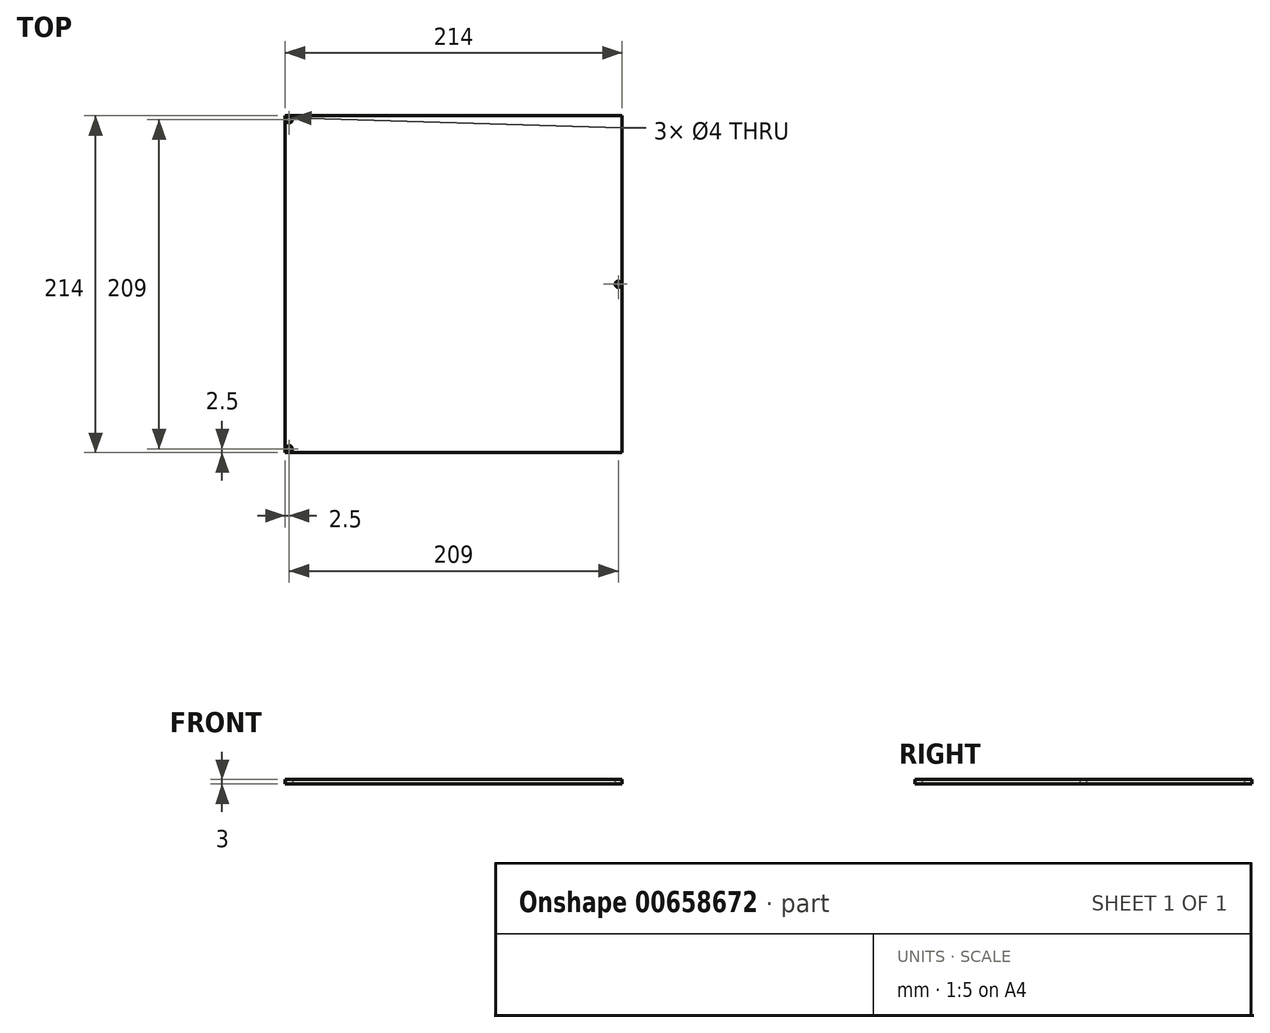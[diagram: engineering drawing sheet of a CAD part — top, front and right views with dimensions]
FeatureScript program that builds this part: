
annotation { "Feature Type Name" : "Feature", "Feature Type Description" : "" }
export const myFeature = defineFeature(function(context is Context, id is Id, definition is map)
    precondition{}
    {
        {
            var Q0;
            Q0=qCreatedBy(makeId("Top.planeOp"),FACE);
            var sketch = newSketch(context, id + "F0", { "sketchPlane" : qUnion([Q0])});
            skLineSegment(sketch, "E0.bottom", {"start": v(107, -107) * mm, "end": v(-107, -107) * mm});
            skLineSegment(sketch, "E0.top", {"start": v(107, 107) * mm, "end": v(-107, 107) * mm});
            skLineSegment(sketch, "E0.left", {"start": v(107, -107) * mm, "end": v(107, 107) * mm});
            skLineSegment(sketch, "E0.right", {"start": v(-107, -107) * mm, "end": v(-107, 107) * mm});
            skPoint(sketch, "E0.middle", {"position": v(0, 0) * mm});
            skSolve(sketch);
        }
        {
            var Q0;
            Q0=makeQuery(id+"F0.imprint","IMPRINT",FACE,{"disambiguationData":[TD([[makeQuery(id+"F0.imprint","IMPRINT",EDGE,{"derivedFrom":sQuery(id+"F0.wireOp",EDGE,"E0.bottom")}),-1.0]])]});
            extrude(context, id + "F1", {"entities" : qUnion([Q0]), "depth" : 3 * mm, "offsetDistance" : 25 * mm});
        }
        {
            var Q0;
            Q0=makeQuery(id+"F1.opExtrude","CAP_FACE",FACE,{"disambiguationData":[OSD([sQuery(id+"F0.wireOp",EDGE,"E0.bottom"),sQuery(id+"F0.wireOp",EDGE,"E0.top"),sQuery(id+"F0.wireOp",EDGE,"E0.left"),sQuery(id+"F0.wireOp",EDGE,"E0.right")])],"isStart":true});
            var sketch = newSketch(context, id + "F2", { "sketchPlane" : qUnion([Q0])});
            skCircle(sketch, "E1", {"center": v(-104.5, 104.5) * mm, "radius": 2 * mm});
            skCircle(sketch, "E2", {"center": v(-104.5, -104.5) * mm, "radius": 2 * mm});
            skCircle(sketch, "E3", {"center": v(104.5, 0) * mm, "radius": 2 * mm});
            skPoint(sketch, "E3.centerSnap0", {"position": v(107, 0) * mm});
            skSolve(sketch);
        }
        {
            var Q0;
            Q0=makeQuery(id+"F2.imprint","IMPRINT",FACE,{"disambiguationData":[TD([[makeQuery(id+"F2.imprint","IMPRINT",EDGE,{"derivedFrom":sQuery(id+"F2.wireOp",EDGE,"E2")}),1.0]])]});
            var Q1;
            Q1=makeQuery(id+"F2.imprint","IMPRINT",FACE,{"disambiguationData":[TD([[makeQuery(id+"F2.imprint","IMPRINT",EDGE,{"derivedFrom":sQuery(id+"F2.wireOp",EDGE,"E1")}),1.0]])]});
            var Q2;
            Q2=makeQuery(id+"F2.imprint","IMPRINT",FACE,{"disambiguationData":[TD([[makeQuery(id+"F2.imprint","IMPRINT",EDGE,{"derivedFrom":sQuery(id+"F2.wireOp",EDGE,"E3")}),1.0]])]});
            extrude(context, id + "F3", {"entities" : qUnion([Q0, Q1, Q2]), "operationType" : NewBodyOperationType.REMOVE, "endBound" : BoundingType.THROUGH_ALL, "oppositeDirection" : true, "depth" : 25 * mm, "offsetDistance" : 25 * mm});
        }
    });
